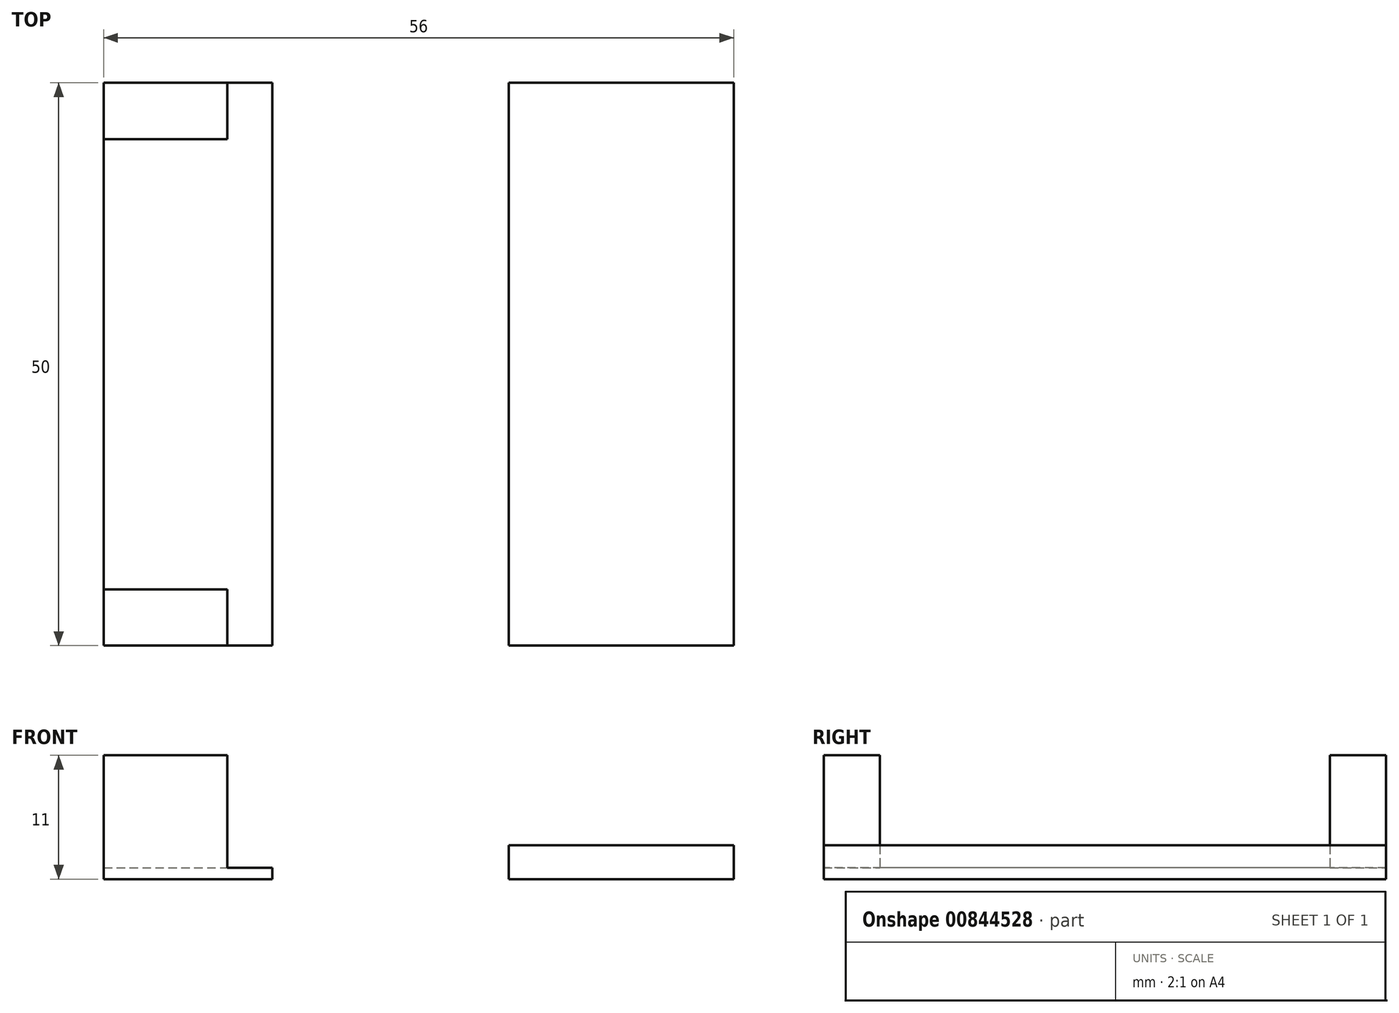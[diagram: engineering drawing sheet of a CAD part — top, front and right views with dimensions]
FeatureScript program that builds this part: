
annotation { "Feature Type Name" : "Feature", "Feature Type Description" : "" }
export const myFeature = defineFeature(function(context is Context, id is Id, definition is map)
    precondition{}
    {
        {
            var Q0;
            Q0=qCreatedBy(makeId("Top.planeOp"),FACE);
            var sketch = newSketch(context, id + "F0", { "sketchPlane" : qUnion([Q0])});
            skLineSegment(sketch, "E0.bottom", {"start": v(-6, 25) * mm, "end": v(9, 25) * mm});
            skLineSegment(sketch, "E0.top", {"start": v(-6, -25) * mm, "end": v(9, -25) * mm});
            skLineSegment(sketch, "E0.left", {"start": v(-6, 25) * mm, "end": v(-6, -25) * mm});
            skLineSegment(sketch, "E0.right", {"start": v(9, 25) * mm, "end": v(9, -25) * mm});
            skSolve(sketch);
        }
        {
            var Q0;
            Q0 = qSketchRegion(id + "F0", true);
            extrude(context, id + "F1", {"entities" : qUnion([Q0]), "depth" : 1 * mm, "offsetDistance" : 25 * mm});
        }
        {
            var Q0;
            Q0=makeQuery(id+"F1.opExtrude","CAP_FACE",FACE,{"disambiguationData":[OSD([sQuery(id+"F0.wireOp",EDGE,"E0.bottom"),sQuery(id+"F0.wireOp",EDGE,"E0.top"),sQuery(id+"F0.wireOp",EDGE,"E0.left"),sQuery(id+"F0.wireOp",EDGE,"E0.right")])],"isStart":false});
            var sketch = newSketch(context, id + "F2", { "sketchPlane" : qUnion([Q0])});
            skLineSegment(sketch, "E1", {"start": v(-6, 20) * mm, "end": v(9, 20) * mm});
            skLineSegment(sketch, "E2", {"start": v(-6, -20) * mm, "end": v(9, -20) * mm});
            skLineSegment(sketch, "E3", {"start": v(5, 20) * mm, "end": v(5, 25) * mm});
            skLineSegment(sketch, "E4", {"start": v(5, -25) * mm, "end": v(5, -20) * mm});
            skSolve(sketch);
        }
        {
            var Q0;
            Q0 = qSketchRegion(id + "F2", true);
            var Q1;
            {var subQ3=sQuery(id+"F2.wireOp",EDGE,"E4");Q1=makeQuery(id+"F2.imprint","IMPRINT",FACE,{"disambiguationData":[TD([[makeQuery(id+"F2.imprint","IMPRINT",EDGE,{"derivedFrom":subQ3}),1.0]])]});}
            var Q2;
            {var subQ3=sQuery(id+"F2.wireOp",EDGE,"E3");Q2=makeQuery(id+"F2.imprint","IMPRINT",FACE,{"disambiguationData":[TD([[makeQuery(id+"F2.imprint","IMPRINT",EDGE,{"derivedFrom":subQ3}),1.0]])]});}
            extrude(context, id + "F3", {"entities" : qUnion([Q0, Q1, Q2]), "operationType" : NewBodyOperationType.ADD, "depth" : 10 * mm, "offsetDistance" : 25 * mm});
        }
        {
            var Q0;
            Q0=qCreatedBy(makeId("Top.planeOp"),FACE);
            var sketch = newSketch(context, id + "F4", { "sketchPlane" : qUnion([Q0])});
            skLineSegment(sketch, "E5.bottom", {"start": v(30, 25) * mm, "end": v(50, 25) * mm});
            skLineSegment(sketch, "E5.top", {"start": v(30, -25) * mm, "end": v(50, -25) * mm});
            skLineSegment(sketch, "E5.left", {"start": v(30, 25) * mm, "end": v(30, -25) * mm});
            skLineSegment(sketch, "E5.right", {"start": v(50, 25) * mm, "end": v(50, -25) * mm});
            skSolve(sketch);
        }
        {
            var Q0;
            Q0=makeQuery(id+"F4.imprint","IMPRINT",FACE,{"disambiguationData":[TD([[makeQuery(id+"F4.imprint","IMPRINT",EDGE,{"derivedFrom":sQuery(id+"F4.wireOp",EDGE,"E5.bottom")}),-1.0]])]});
            extrude(context, id + "F5", {"entities" : qUnion([Q0]), "depth" : 3 * mm, "offsetDistance" : 25 * mm});
        }
    });
